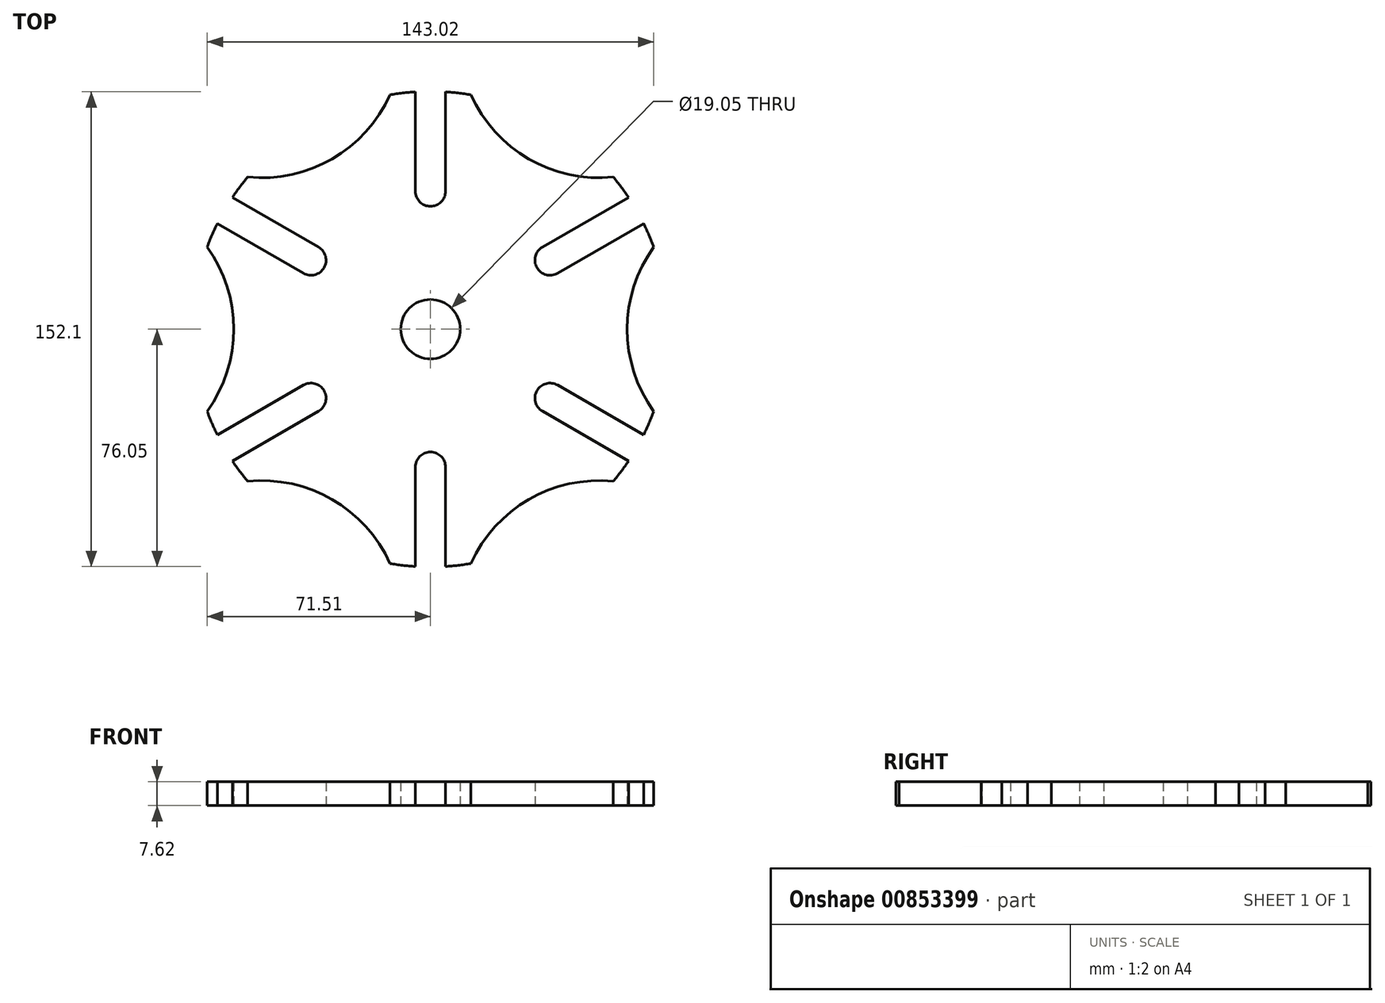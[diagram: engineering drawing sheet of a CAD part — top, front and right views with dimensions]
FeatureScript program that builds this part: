
annotation { "Feature Type Name" : "Feature", "Feature Type Description" : "" }
export const myFeature = defineFeature(function(context is Context, id is Id, definition is map)
    precondition{}
    {
        {
            var Q0;
            Q0=qCreatedBy(makeId("Top.planeOp"),FACE);
            var sketch = newSketch(context, id + "F0", { "sketchPlane" : qUnion([Q0])});
            skCircle(sketch, "E0", {"center": v(0, 0) * mm, "radius": 76.2 * mm});
            skCircle(sketch, "E1", {"center": v(0, 0) * mm, "radius": 9.52 * mm});
            skArc(sketch, "E2", {"start": v(-4.83, 44.2) * mm, "mid": v(0, 39.37) * mm, "end": v(4.83, 44.2) * mm});
            skLineSegment(sketch, "E3", {"start": v(0, 0) * mm, "end": v(0, 76.2) * mm, "construction": true});
            skLineSegment(sketch, "E4", {"start": v(4.83, 44.2) * mm, "end": v(4.83, 76.05) * mm});
            skLineSegment(sketch, "E5.MirrorCS", {"start": v(-4.83, 44.2) * mm, "end": v(-4.83, 76.05) * mm});
            skLineSegment(sketch, "E6.1.0", {"start": v(-40.69, 17.92) * mm, "end": v(-68.27, 33.84) * mm});
            skArc(sketch, "E6.1.1", {"start": v(-40.69, 17.92) * mm, "mid": v(-34.1, 19.69) * mm, "end": v(-35.86, 26.28) * mm});
            skLineSegment(sketch, "E6.1.2", {"start": v(-35.86, 26.28) * mm, "end": v(-63.45, 42.2) * mm});
            skLineSegment(sketch, "E6.2.0", {"start": v(-35.86, -26.28) * mm, "end": v(-63.45, -42.2) * mm});
            skArc(sketch, "E6.2.1", {"start": v(-35.86, -26.28) * mm, "mid": v(-34.1, -19.68) * mm, "end": v(-40.69, -17.92) * mm});
            skLineSegment(sketch, "E6.2.2", {"start": v(-40.69, -17.92) * mm, "end": v(-68.27, -33.84) * mm});
            skLineSegment(sketch, "E6.3.0", {"start": v(4.83, -44.2) * mm, "end": v(4.83, -76.05) * mm});
            skArc(sketch, "E6.3.1", {"start": v(4.83, -44.2) * mm, "mid": v(0, -39.37) * mm, "end": v(-4.83, -44.2) * mm});
            skLineSegment(sketch, "E6.3.2", {"start": v(-4.83, -44.2) * mm, "end": v(-4.83, -76.05) * mm});
            skLineSegment(sketch, "E6.4.0", {"start": v(40.69, -17.92) * mm, "end": v(68.27, -33.84) * mm});
            skArc(sketch, "E6.4.1", {"start": v(40.69, -17.92) * mm, "mid": v(34.1, -19.69) * mm, "end": v(35.86, -26.28) * mm});
            skLineSegment(sketch, "E6.4.2", {"start": v(35.86, -26.28) * mm, "end": v(63.45, -42.2) * mm});
            skLineSegment(sketch, "E6.5.0", {"start": v(35.86, 26.28) * mm, "end": v(63.45, 42.2) * mm});
            skArc(sketch, "E6.5.1", {"start": v(35.86, 26.28) * mm, "mid": v(34.1, 19.69) * mm, "end": v(40.69, 17.92) * mm});
            skLineSegment(sketch, "E6.5.2", {"start": v(40.69, 17.92) * mm, "end": v(68.27, 33.84) * mm});
            skArc(sketch, "E7.1.10", {"start": v(35.86, 26.28) * mm, "mid": v(34.1, 19.68) * mm, "end": v(40.69, 17.92) * mm});
            skArc(sketch, "E7.2.1", {"start": v(35.86, 26.28) * mm, "mid": v(34.1, 19.68) * mm, "end": v(40.69, 17.92) * mm});
            skArc(sketch, "E8", {"start": v(71.5, 26.33) * mm, "mid": v(63, 0) * mm, "end": v(71.5, -26.33) * mm});
            skArc(sketch, "E9.1.0", {"start": v(12.95, 75.1) * mm, "mid": v(31.5, 54.55) * mm, "end": v(58.55, 48.76) * mm});
            skArc(sketch, "E9.2.0", {"start": v(-58.55, 48.76) * mm, "mid": v(-31.5, 54.55) * mm, "end": v(-12.95, 75.1) * mm});
            skArc(sketch, "E9.3.0", {"start": v(-71.5, -26.33) * mm, "mid": v(-63, 0) * mm, "end": v(-71.5, 26.33) * mm});
            skArc(sketch, "E9.4.0", {"start": v(-12.95, -75.1) * mm, "mid": v(-31.5, -54.55) * mm, "end": v(-58.55, -48.76) * mm});
            skArc(sketch, "E9.5.0", {"start": v(58.55, -48.76) * mm, "mid": v(31.5, -54.55) * mm, "end": v(12.95, -75.1) * mm});
            skSolve(sketch);
        }
        {
            var Q0;
            Q0=makeQuery(id+"F0.imprint","IMPRINT",FACE,{"disambiguationData":[TD([[makeQuery(id+"F0.imprint","IMPRINT",EDGE,{"derivedFrom":sQuery(id+"F0.wireOp",EDGE,"E1")}),-1.0]])]});
            extrude(context, id + "F1", {"entities" : qUnion([Q0]), "depth" : 7.62 * mm, "offsetDistance" : 25.4 * mm});
        }
    });
